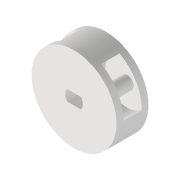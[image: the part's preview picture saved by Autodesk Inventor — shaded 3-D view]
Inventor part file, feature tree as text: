
AUTODESK INVENTOR PART (.ipt)
format: ipt  version: 2022.5 (Build 265521000, 521)  size: 242,688 bytes
history: native  units: mm
features: extrude x3, sketch x2, other x2, mirror x1, projected_geometry x1, reference x1
ambient origin geometry x8: Origin, YZ Plane, XZ Plane, XY Plane, X Axis, Y Axis, Z Axis, Center Point
bodies: Body1 (feature_tree)
feature tree (10):
  extrude  "Extrusion3"  Depth=9.5mm
  extrude  "Extrusion4"  Depth=2.0mm
  extrude  "Extrusion7"  Depth=2.0mm
  mirror  "Spiegeln1"
  sketch  "Skizze3"  dims[d10=25.0mm d11=9.5mm]
  projected_geometry  "Projizierte Kontur1"
  reference  "Referenz1"
  sketch  "Skizze9"  dims[d12=3.8mm d13=3.8mm d14=3.8mm d15=5.2mm d16=1.6mm d17=1.6mm d18=2.0mm d19=0.0mm d20=13.0mm d21=13.0mm d22=13.0mm d23=2.7mm d24=0.0mm d40=2.7mm d41=2.0mm d42=0.0mm d43=0.0mm]
  other  "Planktoscope_Mini_Peristalticpump_new.iam"
  other  "00_Bearing_4x13x5:1"
